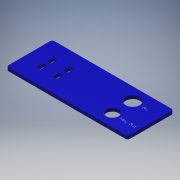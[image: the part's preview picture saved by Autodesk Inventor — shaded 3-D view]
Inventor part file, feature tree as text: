
AUTODESK INVENTOR PART (.ipt)
format: ipt  version: 2016 (Build 200138000, 138)  size: 256,512 bytes
history: native  units: mm
features: sketch x5, other x4, extrude x3, fillet x1
ambient origin geometry x8: Origin, YZ Plane, XZ Plane, XY Plane, X Axis, Y Axis, Z Axis, Center Point
bodies: Solid1 (feature_tree)
feature tree (13):
  extrude  "Extrusion1"  Depth=22.5mm
  fillet  "Fillet1"  Radius=1.6mm
  extrude  "Extrusion2"  Depth=1.0mm
  extrude  "Extrusion3"  Depth=1.8mm
  other  "Decal1"
  other  "Decal2"
  sketch  "Sketch1"  dims[d0=59.5mm d1=22.5mm d2=1.6mm d3=0.0mm]
  sketch  "Sketch2"  dims[d4=1.0mm d5=17.0mm]
  sketch  "Sketch3"  dims[d6=1.8mm d7=0.9mm]
  sketch  "Sketch4"  dims[d8=0.0mm]
  other  "Image1"
  sketch  "Sketch5"  dims[d10=1.8mm d11=1.8mm d12=3.2mm d13=3.2mm d14=1.6mm d15=0.0mm d16=4.0mm d17=8.75mm d18=7.0mm d19=6.0mm d20=10.0mm d21=5.0mm d22=16.0mm d23=10.0mm d24=0.0mm d25=45.75mm d26=6.25mm d27=16.25mm d28=11.25mm d29=16.75mm]
  other  "Image2"
